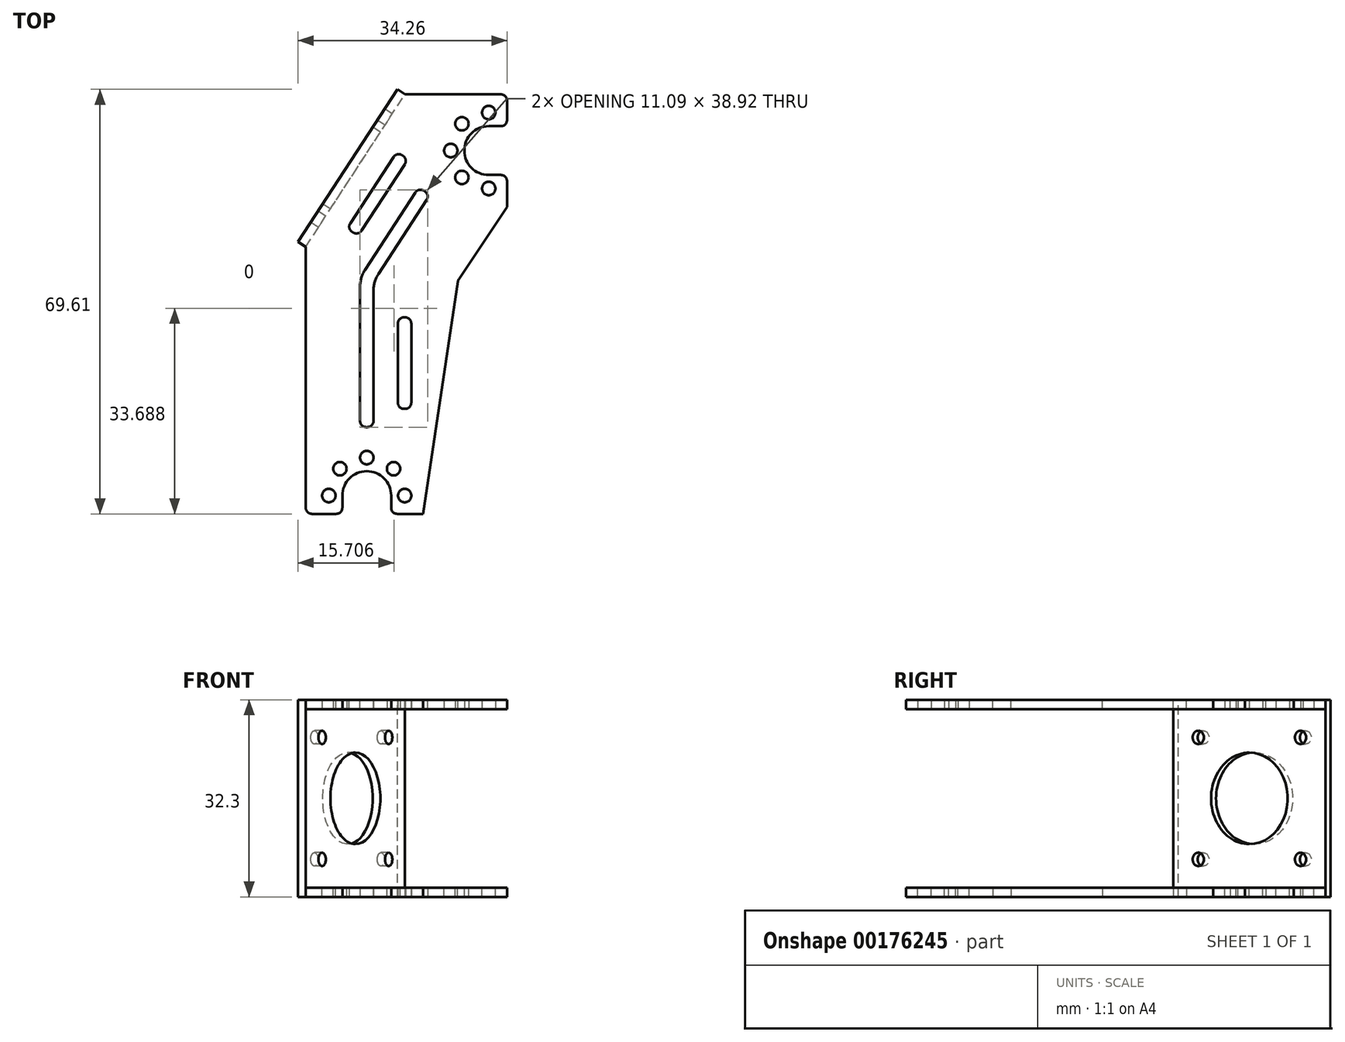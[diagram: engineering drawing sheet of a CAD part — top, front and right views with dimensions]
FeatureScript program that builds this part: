
annotation { "Feature Type Name" : "Feature", "Feature Type Description" : "" }
export const myFeature = defineFeature(function(context is Context, id is Id, definition is map)
    precondition{}
    {
        {
            var Q0;
            Q0=qCreatedBy(makeId("Top.planeOp"),FACE);
            var sketch = newSketch(context, id + "F0", { "sketchPlane" : qUnion([Q0])});
            skLineSegment(sketch, "E0.bottom", {"start": v(-16.5, 34.4) * mm, "end": v(16.5, 34.4) * mm});
            skLineSegment(sketch, "E0.top", {"start": v(-16.5, -34.4) * mm, "end": v(-10.5, -34.4) * mm});
            skLineSegment(sketch, "E0.left", {"start": v(-16.5, 34.4) * mm, "end": v(-16.5, -34.4) * mm});
            skLineSegment(sketch, "E0.right", {"start": v(16.5, 34.4) * mm, "end": v(16.5, 29.17) * mm});
            skPoint(sketch, "E0.middle", {"position": v(0, 0) * mm});
            skArc(sketch, "E1", {"start": v(13.5, 29.17) * mm, "mid": v(9.5, 25.17) * mm, "end": v(13.5, 21.17) * mm});
            skArc(sketch, "E2", {"start": v(-2.5, -31.4) * mm, "mid": v(-6.5, -27.4) * mm, "end": v(-10.5, -31.4) * mm});
            skLineSegment(sketch, "E3.bottom", {"start": v(9.1, 29.57) * mm, "end": v(17.9, 29.57) * mm, "construction": true});
            skLineSegment(sketch, "E3.top", {"start": v(9.1, 20.77) * mm, "end": v(17.9, 20.77) * mm, "construction": true});
            skLineSegment(sketch, "E3.left", {"start": v(9.1, 29.57) * mm, "end": v(9.1, 20.77) * mm, "construction": true});
            skLineSegment(sketch, "E3.right", {"start": v(17.9, 29.57) * mm, "end": v(17.9, 20.77) * mm, "construction": true});
            skCircle(sketch, "E4", {"center": v(9.1, 29.57) * mm, "radius": 1.1 * mm});
            skCircle(sketch, "E5.1.0", {"center": v(7.28, 25.17) * mm, "radius": 1.1 * mm});
            skCircle(sketch, "E5.2.0", {"center": v(9.1, 20.77) * mm, "radius": 1.1 * mm});
            skCircle(sketch, "E5.3.0", {"center": v(13.5, 18.95) * mm, "radius": 1.1 * mm});
            skCircle(sketch, "E5.7.0", {"center": v(13.5, 31.4) * mm, "radius": 1.1 * mm});
            skLineSegment(sketch, "E6.bottom", {"start": v(-10.9, -27) * mm, "end": v(-2.1, -27) * mm, "construction": true});
            skLineSegment(sketch, "E6.top", {"start": v(-10.9, -35.8) * mm, "end": v(-2.1, -35.8) * mm, "construction": true});
            skLineSegment(sketch, "E6.left", {"start": v(-10.9, -27) * mm, "end": v(-10.9, -35.8) * mm, "construction": true});
            skLineSegment(sketch, "E6.right", {"start": v(-2.1, -27) * mm, "end": v(-2.1, -35.8) * mm, "construction": true});
            skCircle(sketch, "E7", {"center": v(-2.1, -27) * mm, "radius": 1.1 * mm});
            skCircle(sketch, "E8.1.0", {"center": v(-6.5, -25.17) * mm, "radius": 1.1 * mm});
            skCircle(sketch, "E8.2.0", {"center": v(-10.9, -27) * mm, "radius": 1.1 * mm});
            skCircle(sketch, "E8.3.0", {"center": v(-12.72, -31.4) * mm, "radius": 1.1 * mm});
            skCircle(sketch, "E8.7.0", {"center": v(-0.28, -31.4) * mm, "radius": 1.1 * mm});
            skLineSegment(sketch, "E9", {"start": v(13.5, 29.17) * mm, "end": v(16.5, 29.17) * mm});
            skLineSegment(sketch, "E10", {"start": v(13.5, 21.17) * mm, "end": v(16.5, 21.17) * mm});
            skLineSegment(sketch, "E11.trimOffspring", {"start": v(16.5, 21.17) * mm, "end": v(16.5, -34.4) * mm});
            skLineSegment(sketch, "E12", {"start": v(-2.5, -31.4) * mm, "end": v(-2.5, -34.4) * mm});
            skLineSegment(sketch, "E13", {"start": v(-10.5, -31.4) * mm, "end": v(-10.5, -34.4) * mm});
            skLineSegment(sketch, "E14.trimOffspring", {"start": v(-2.5, -34.4) * mm, "end": v(16.5, -34.4) * mm});
            skSolve(sketch);
        }
        {
            var Q0;
            Q0=qSketchRegion(id+"F0",true);
            extrude(context, id + "F1", {"entities" : qUnion([Q0]), "depth" : 1.5 * mm});
        }
        {
            var Q0;
            Q0=makeQuery(id+"F1.opExtrude","CAP_FACE",FACE,{"disambiguationData":[OSD([sQuery(id+"F0.wireOp",EDGE,"E0.bottom"),sQuery(id+"F0.wireOp",EDGE,"E0.top"),sQuery(id+"F0.wireOp",EDGE,"E0.left"),sQuery(id+"F0.wireOp",EDGE,"E0.right"),sQuery(id+"F0.wireOp",EDGE,"E1"),sQuery(id+"F0.wireOp",EDGE,"E2"),sQuery(id+"F0.wireOp",EDGE,"E4"),sQuery(id+"F0.wireOp",EDGE,"E5.1.0"),sQuery(id+"F0.wireOp",EDGE,"E5.2.0"),sQuery(id+"F0.wireOp",EDGE,"E5.3.0"),sQuery(id+"F0.wireOp",EDGE,"E5.7.0"),sQuery(id+"F0.wireOp",EDGE,"E7"),sQuery(id+"F0.wireOp",EDGE,"E8.1.0"),sQuery(id+"F0.wireOp",EDGE,"E8.2.0"),sQuery(id+"F0.wireOp",EDGE,"E8.3.0"),sQuery(id+"F0.wireOp",EDGE,"E8.7.0"),sQuery(id+"F0.wireOp",EDGE,"E9"),sQuery(id+"F0.wireOp",EDGE,"E10"),sQuery(id+"F0.wireOp",EDGE,"E11.trimOffspring"),sQuery(id+"F0.wireOp",EDGE,"E12"),sQuery(id+"F0.wireOp",EDGE,"E13"),sQuery(id+"F0.wireOp",EDGE,"E14.trimOffspring")])],"isStart":false});
            var sketch = newSketch(context, id + "F2", { "sketchPlane" : qUnion([Q0])});
            skPoint(sketch, "E15", {"position": v(7.28, 25.17) * mm});
            skPoint(sketch, "E16", {"position": v(-0.28, -31.4) * mm});
            skLineSegment(sketch, "E17", {"start": v(-0.22, 34.4) * mm, "end": v(-16.5, 9.4) * mm});
            skPoint(sketch, "E18", {"position": v(13.5, 18.95) * mm});
            skLineSegment(sketch, "E19", {"start": v(16.5, 15.95) * mm, "end": v(8.5, 3.95) * mm});
            skLineSegment(sketch, "E20", {"start": v(8.5, 3.95) * mm, "end": v(2.72, -34.4) * mm});
            skPoint(sketch, "E21", {"position": v(13.5, 25.17) * mm});
            skPoint(sketch, "E22", {"position": v(-6.5, -31.4) * mm});
            skLineSegment(sketch, "E23", {"start": v(13.5, 25.17) * mm, "end": v(-6.5, -31.4) * mm, "construction": true});
            skLineSegment(sketch, "E24", {"start": v(0.31, -7.62) * mm, "end": v(-2.35, -15.17) * mm});
            skPoint(sketch, "E25", {"position": v(-1.02, -11.4) * mm});
            skLineSegment(sketch, "E26", {"start": v(1.59, -7.01) * mm, "end": v(2.06, -7.18) * mm});
            skLineSegment(sketch, "E27", {"start": v(-1.74, -16.44) * mm, "end": v(-1.27, -16.6) * mm});
            skLineSegment(sketch, "E28.MirrorCS", {"start": v(2.53, -7.35) * mm, "end": v(2.06, -7.18) * mm});
            skLineSegment(sketch, "E29.MirrorCS", {"start": v(3.14, -8.62) * mm, "end": v(0.48, -16.17) * mm});
            skLineSegment(sketch, "E30.MirrorCS", {"start": v(-0.8, -16.78) * mm, "end": v(-1.27, -16.6) * mm});
            skPoint(sketch, "E31.visualSharp", {"position": v(0.65, -6.68) * mm});
            skArc(sketch, "E31.filletArc", {"start": v(1.59, -7.01) * mm, "mid": v(0.83, -7.06) * mm, "end": v(0.31, -7.62) * mm});
            skPoint(sketch, "E32.visualSharp", {"position": v(-2.69, -16.1) * mm});
            skArc(sketch, "E32.filletArc", {"start": v(-2.35, -15.17) * mm, "mid": v(-2.31, -15.93) * mm, "end": v(-1.74, -16.44) * mm});
            skPoint(sketch, "E33.visualSharp", {"position": v(3.48, -7.68) * mm});
            skArc(sketch, "E33.filletArc", {"start": v(3.14, -8.62) * mm, "mid": v(3.1, -7.86) * mm, "end": v(2.53, -7.35) * mm});
            skPoint(sketch, "E34.visualSharp", {"position": v(0.14, -17.1) * mm});
            skArc(sketch, "E34.filletArc", {"start": v(-0.8, -16.78) * mm, "mid": v(-0.04, -16.74) * mm, "end": v(0.48, -16.17) * mm});
            skSolve(sketch);
        }
        {
            var Q0;
            {var subQ0=sQuery(id+"F2.wireOp",EDGE,"E19");Q0=makeQuery(id+"F2.imprint","IMPRINT",FACE,{"disambiguationData":[TD([[makeQuery(id+"F2.imprint","IMPRINT",EDGE,{"derivedFrom":subQ0}),1.0]])]});}
            var Q1;
            {var subQ0=sQuery(id+"F2.wireOp",EDGE,"E17");Q1=makeQuery(id+"F2.imprint","IMPRINT",FACE,{"disambiguationData":[TD([[makeQuery(id+"F2.imprint","IMPRINT",EDGE,{"derivedFrom":subQ0}),-1.0]])]});}
            extrude(context, id + "F3", {"entities" : qUnion([Q0, Q1]), "operationType" : NewBodyOperationType.REMOVE, "endBound" : BoundingType.UP_TO_NEXT, "oppositeDirection" : true, "depth" : 25 * mm});
        }
        {
            var Q0;
            Q0=makeQuery(id+"F1.opExtrude","CAP_FACE",FACE,{"disambiguationData":[OSD([sQuery(id+"F0.wireOp",EDGE,"E0.bottom"),sQuery(id+"F0.wireOp",EDGE,"E0.top"),sQuery(id+"F0.wireOp",EDGE,"E0.left"),sQuery(id+"F0.wireOp",EDGE,"E0.right"),sQuery(id+"F0.wireOp",EDGE,"E1"),sQuery(id+"F0.wireOp",EDGE,"E2"),sQuery(id+"F0.wireOp",EDGE,"E4"),sQuery(id+"F0.wireOp",EDGE,"E5.1.0"),sQuery(id+"F0.wireOp",EDGE,"E5.2.0"),sQuery(id+"F0.wireOp",EDGE,"E5.3.0"),sQuery(id+"F0.wireOp",EDGE,"E5.7.0"),sQuery(id+"F0.wireOp",EDGE,"E7"),sQuery(id+"F0.wireOp",EDGE,"E8.1.0"),sQuery(id+"F0.wireOp",EDGE,"E8.2.0"),sQuery(id+"F0.wireOp",EDGE,"E8.3.0"),sQuery(id+"F0.wireOp",EDGE,"E8.7.0"),sQuery(id+"F0.wireOp",EDGE,"E9"),sQuery(id+"F0.wireOp",EDGE,"E10"),sQuery(id+"F0.wireOp",EDGE,"E11.trimOffspring"),sQuery(id+"F0.wireOp",EDGE,"E12"),sQuery(id+"F0.wireOp",EDGE,"E13"),sQuery(id+"F0.wireOp",EDGE,"E14.trimOffspring")])],"isStart":false});
            var sketch = newSketch(context, id + "F4", { "sketchPlane" : qUnion([Q0])});
            skPoint(sketch, "E35", {"position": v(13.5, 25.17) * mm});
            skPoint(sketch, "E36", {"position": v(-6.5, -31.4) * mm});
            skPoint(sketch, "E37", {"position": v(7.28, 25.17) * mm});
            skPoint(sketch, "E38", {"position": v(-6.5, -25.17) * mm});
            skLineSegment(sketch, "E39", {"start": v(-6.5, -25.17) * mm, "end": v(-6.5, 4.01) * mm, "construction": true});
            skLineSegment(sketch, "E40", {"start": v(-6.5, 4.01) * mm, "end": v(7.28, 25.17) * mm, "construction": true});
            skLineSegment(sketch, "E41", {"start": v(1.49, 18.3) * mm, "end": v(-6.8, 5.58) * mm});
            skLineSegment(sketch, "E42", {"start": v(-7.6, 2.85) * mm, "end": v(-7.6, -19.17) * mm});
            skLineSegment(sketch, "E43", {"start": v(2.87, 18.59) * mm, "end": v(2.95, 18.53) * mm});
            skLineSegment(sketch, "E44", {"start": v(-6.6, -20.17) * mm, "end": v(-6.5, -20.17) * mm});
            skLineSegment(sketch, "E45.MirrorCS", {"start": v(-6.4, -20.17) * mm, "end": v(-6.5, -20.17) * mm});
            skLineSegment(sketch, "E46.MirrorCS", {"start": v(-5.4, 2.2) * mm, "end": v(-5.4, -19.17) * mm});
            skLineSegment(sketch, "E47.MirrorCS", {"start": v(3.33, 17.1) * mm, "end": v(-4.6, 4.93) * mm});
            skLineSegment(sketch, "E48.MirrorCS", {"start": v(3.04, 18.48) * mm, "end": v(2.95, 18.53) * mm});
            skPoint(sketch, "E49.orphan", {"position": v(-5.4, 4.34) * mm});
            skPoint(sketch, "E50.orphan", {"position": v(-5.76, 3.14) * mm});
            skPoint(sketch, "E51.visualSharp", {"position": v(2.03, 19.13) * mm});
            skArc(sketch, "E51.filletArc", {"start": v(2.87, 18.59) * mm, "mid": v(2.12, 18.73) * mm, "end": v(1.49, 18.3) * mm});
            skPoint(sketch, "E52.visualSharp", {"position": v(3.88, 17.93) * mm});
            skArc(sketch, "E52.filletArc", {"start": v(3.33, 17.1) * mm, "mid": v(3.47, 17.85) * mm, "end": v(3.04, 18.48) * mm});
            skPoint(sketch, "E53.visualSharp", {"position": v(-7.6, -20.17) * mm});
            skArc(sketch, "E53.filletArc", {"start": v(-7.6, -19.17) * mm, "mid": v(-7.3, -19.88) * mm, "end": v(-6.6, -20.17) * mm});
            skPoint(sketch, "E54.visualSharp", {"position": v(-5.4, -20.17) * mm});
            skArc(sketch, "E54.filletArc", {"start": v(-6.4, -20.17) * mm, "mid": v(-5.7, -19.88) * mm, "end": v(-5.4, -19.17) * mm});
            skPoint(sketch, "E55.visualSharp", {"position": v(-7.6, 4.34) * mm});
            skArc(sketch, "E55.filletArc", {"start": v(-6.8, 5.58) * mm, "mid": v(-7.4, 4.28) * mm, "end": v(-7.6, 2.85) * mm});
            skPoint(sketch, "E56.visualSharp", {"position": v(-5.4, 3.69) * mm});
            skArc(sketch, "E56.filletArc", {"start": v(-4.6, 4.93) * mm, "mid": v(-5.2, 3.62) * mm, "end": v(-5.4, 2.2) * mm});
            skLineSegment(sketch, "E57", {"start": v(-0.27, 22.93) * mm, "end": v(-7.36, 12.03) * mm});
            skLineSegment(sketch, "E58", {"start": v(-8.75, 11.74) * mm, "end": v(-8.91, 11.85) * mm});
            skLineSegment(sketch, "E59", {"start": v(-0.56, 24.31) * mm, "end": v(-0.73, 24.42) * mm});
            skLineSegment(sketch, "E60", {"start": v(-2.11, 24.13) * mm, "end": v(-9.2, 13.23) * mm});
            skPoint(sketch, "E61.visualSharp", {"position": v(-1.57, 24.97) * mm});
            skArc(sketch, "E61.filletArc", {"start": v(-0.73, 24.42) * mm, "mid": v(-1.48, 24.56) * mm, "end": v(-2.11, 24.13) * mm});
            skPoint(sketch, "E62.visualSharp", {"position": v(-9.75, 12.4) * mm});
            skArc(sketch, "E62.filletArc", {"start": v(-9.2, 13.23) * mm, "mid": v(-9.35, 12.48) * mm, "end": v(-8.91, 11.85) * mm});
            skPoint(sketch, "E63.visualSharp", {"position": v(0.28, 23.77) * mm});
            skArc(sketch, "E63.filletArc", {"start": v(-0.27, 22.93) * mm, "mid": v(-0.13, 23.68) * mm, "end": v(-0.56, 24.31) * mm});
            skPoint(sketch, "E64.visualSharp", {"position": v(-7.9, 11.2) * mm});
            skArc(sketch, "E64.filletArc", {"start": v(-8.75, 11.74) * mm, "mid": v(-8, 11.6) * mm, "end": v(-7.36, 12.03) * mm});
            skLineSegment(sketch, "E65.bottom", {"start": v(-0.4, -2.17) * mm, "end": v(-0.2, -2.17) * mm});
            skLineSegment(sketch, "E65.top", {"start": v(-0.4, -17.17) * mm, "end": v(-0.2, -17.17) * mm});
            skLineSegment(sketch, "E65.left", {"start": v(-1.4, -3.17) * mm, "end": v(-1.4, -16.17) * mm});
            skLineSegment(sketch, "E65.right", {"start": v(0.8, -3.17) * mm, "end": v(0.8, -16.17) * mm});
            skPoint(sketch, "E65.middle", {"position": v(-0.3, -9.67) * mm});
            skPoint(sketch, "E66.visualSharp", {"position": v(-1.4, -2.17) * mm});
            skArc(sketch, "E66.filletArc", {"start": v(-0.4, -2.17) * mm, "mid": v(-1.1, -2.47) * mm, "end": v(-1.4, -3.17) * mm});
            skPoint(sketch, "E67.visualSharp", {"position": v(-1.4, -17.17) * mm});
            skArc(sketch, "E67.filletArc", {"start": v(-1.4, -16.17) * mm, "mid": v(-1.1, -16.88) * mm, "end": v(-0.4, -17.17) * mm});
            skPoint(sketch, "E68.visualSharp", {"position": v(0.8, -17.17) * mm});
            skArc(sketch, "E68.filletArc", {"start": v(-0.2, -17.17) * mm, "mid": v(0.5, -16.88) * mm, "end": v(0.8, -16.17) * mm});
            skPoint(sketch, "E69.visualSharp", {"position": v(0.8, -2.17) * mm});
            skArc(sketch, "E69.filletArc", {"start": v(0.8, -3.17) * mm, "mid": v(0.5, -2.47) * mm, "end": v(-0.2, -2.17) * mm});
            skLineSegment(sketch, "E70.MirrorCS", {"start": v(1.48, 5.08) * mm, "end": v(1.64, 4.98) * mm, "construction": true});
            skLineSegment(sketch, "E71.MirrorCS", {"start": v(9.66, 17.65) * mm, "end": v(9.83, 17.55) * mm, "construction": true});
            skArc(sketch, "E72.MirrorCS", {"start": v(3.03, 5.27) * mm, "mid": v(2.4, 4.83) * mm, "end": v(1.64, 4.98) * mm, "construction": true});
            skArc(sketch, "E73.MirrorCS", {"start": v(8.28, 17.36) * mm, "mid": v(8.9, 17.8) * mm, "end": v(9.66, 17.65) * mm, "construction": true});
            skArc(sketch, "E74.MirrorCS", {"start": v(9.83, 17.55) * mm, "mid": v(10.26, 16.91) * mm, "end": v(10.12, 16.16) * mm, "construction": true});
            skArc(sketch, "E75.MirrorCS", {"start": v(1.48, 5.08) * mm, "mid": v(1.04, 5.72) * mm, "end": v(1.18, 6.47) * mm, "construction": true});
            skLineSegment(sketch, "E76.MirrorCS", {"start": v(10.12, 16.16) * mm, "end": v(3.03, 5.27) * mm, "construction": true});
            skPoint(sketch, "E77.MirrorP", {"position": v(10.67, 17) * mm});
            skPoint(sketch, "E78.MirrorP", {"position": v(8.82, 18.2) * mm});
            skLineSegment(sketch, "E79.MirrorCS", {"start": v(8.28, 17.36) * mm, "end": v(1.18, 6.47) * mm, "construction": true});
            skPoint(sketch, "E80.MirrorP", {"position": v(2.48, 4.43) * mm});
            skPoint(sketch, "E81.MirrorP", {"position": v(0.64, 5.63) * mm});
            skLineSegment(sketch, "E82.MirrorCS", {"start": v(-12.6, -17.17) * mm, "end": v(-12.8, -17.17) * mm, "construction": true});
            skLineSegment(sketch, "E83.MirrorCS", {"start": v(-12.6, -2.17) * mm, "end": v(-12.8, -2.17) * mm, "construction": true});
            skArc(sketch, "E84.MirrorCS", {"start": v(-12.8, -17.17) * mm, "mid": v(-13.5, -16.88) * mm, "end": v(-13.8, -16.17) * mm, "construction": true});
            skArc(sketch, "E85.MirrorCS", {"start": v(-13.8, -3.17) * mm, "mid": v(-13.5, -2.47) * mm, "end": v(-12.8, -2.17) * mm, "construction": true});
            skArc(sketch, "E86.MirrorCS", {"start": v(-12.6, -2.17) * mm, "mid": v(-11.9, -2.47) * mm, "end": v(-11.6, -3.17) * mm, "construction": true});
            skArc(sketch, "E87.MirrorCS", {"start": v(-11.6, -16.17) * mm, "mid": v(-11.9, -16.88) * mm, "end": v(-12.6, -17.17) * mm, "construction": true});
            skPoint(sketch, "E88.MirrorP", {"position": v(-13.8, -17.17) * mm});
            skPoint(sketch, "E89.MirrorP", {"position": v(-13.8, -2.17) * mm});
            skLineSegment(sketch, "E90.MirrorCS", {"start": v(-11.6, -3.17) * mm, "end": v(-11.6, -16.17) * mm, "construction": true});
            skPoint(sketch, "E91.MirrorP", {"position": v(-12.7, -9.67) * mm});
            skPoint(sketch, "E92.MirrorP", {"position": v(-11.6, -2.17) * mm});
            skPoint(sketch, "E93.MirrorP", {"position": v(-11.6, -17.17) * mm});
            skLineSegment(sketch, "E94.MirrorCS", {"start": v(-13.8, -3.17) * mm, "end": v(-13.8, -16.17) * mm, "construction": true});
            skPoint(sketch, "E95.0.1.0", {"position": v(-11.6, -7.17) * mm});
            skPoint(sketch, "E95.0.1.1", {"position": v(-11.6, 7.83) * mm});
            skPoint(sketch, "E95.0.1.2", {"position": v(-12.7, 0.33) * mm});
            skLineSegment(sketch, "E95.0.1.3", {"start": v(-13.8, 6.83) * mm, "end": v(-13.8, -6.17) * mm});
            skPoint(sketch, "E95.0.1.4", {"position": v(-13.8, -7.17) * mm});
            skLineSegment(sketch, "E95.0.1.5", {"start": v(-11.6, 6.83) * mm, "end": v(-11.6, -6.17) * mm});
            skPoint(sketch, "E95.0.1.6", {"position": v(-13.8, 7.83) * mm});
            skArc(sketch, "E95.0.1.7", {"start": v(-12.8, -7.17) * mm, "mid": v(-13.5, -6.88) * mm, "end": v(-13.8, -6.17) * mm});
            skArc(sketch, "E95.0.1.8", {"start": v(-13.8, 6.83) * mm, "mid": v(-13.5, 7.53) * mm, "end": v(-12.8, 7.83) * mm});
            skArc(sketch, "E95.0.1.9", {"start": v(-12.6, 7.83) * mm, "mid": v(-11.9, 7.53) * mm, "end": v(-11.6, 6.83) * mm});
            skArc(sketch, "E95.0.1.10", {"start": v(-11.6, -6.17) * mm, "mid": v(-11.9, -6.88) * mm, "end": v(-12.6, -7.17) * mm});
            skLineSegment(sketch, "E95.0.1.11", {"start": v(-12.6, 7.83) * mm, "end": v(-12.8, 7.83) * mm});
            skLineSegment(sketch, "E95.0.1.12", {"start": v(-12.6, -7.17) * mm, "end": v(-12.8, -7.17) * mm});
            skLineSegment(sketch, "E95.direction1", {"start": v(-13.8, -17.17) * mm, "end": v(11.2, -17.17) * mm, "construction": true});
            skLineSegment(sketch, "E95.direction2", {"start": v(-13.8, -17.17) * mm, "end": v(-13.8, -7.17) * mm, "construction": true});
            skLineSegment(sketch, "E96.1.0.0", {"start": v(2.82, 8.98) * mm, "end": v(-4.27, -1.91) * mm});
            skArc(sketch, "E96.1.0.1", {"start": v(2.82, 8.98) * mm, "mid": v(3.45, 9.41) * mm, "end": v(4.2, 9.27) * mm});
            skArc(sketch, "E96.1.0.2", {"start": v(4.37, 9.17) * mm, "mid": v(4.8, 8.53) * mm, "end": v(4.66, 7.78) * mm});
            skLineSegment(sketch, "E96.1.0.3", {"start": v(4.2, 9.27) * mm, "end": v(4.37, 9.17) * mm});
            skLineSegment(sketch, "E96.1.0.4", {"start": v(4.66, 7.78) * mm, "end": v(-2.43, -3.11) * mm});
            skArc(sketch, "E96.1.0.5", {"start": v(-3.98, -3.3) * mm, "mid": v(-4.41, -2.66) * mm, "end": v(-4.27, -1.91) * mm});
            skLineSegment(sketch, "E96.1.0.6", {"start": v(-3.98, -3.3) * mm, "end": v(-3.81, -3.4) * mm});
            skArc(sketch, "E96.1.0.7", {"start": v(-2.43, -3.11) * mm, "mid": v(-3.06, -3.55) * mm, "end": v(-3.81, -3.4) * mm});
            skLineSegment(sketch, "E96.direction1", {"start": v(-3.98, -3.3) * mm, "end": v(1.48, 5.08) * mm, "construction": true});
            skSolve(sketch);
        }
        {
            var Q0;
            Q0=makeQuery(id+"F4.imprint","IMPRINT",FACE,{"disambiguationData":[TD([[makeQuery(id+"F4.imprint","IMPRINT",EDGE,{"derivedFrom":sQuery(id+"F4.wireOp",EDGE,"E57")}),-1.0]])]});
            var Q1;
            Q1=makeQuery(id+"F4.imprint","IMPRINT",FACE,{"disambiguationData":[TD([[makeQuery(id+"F4.imprint","IMPRINT",EDGE,{"derivedFrom":sQuery(id+"F4.wireOp",EDGE,"E41")}),1.0]])]});
            var Q2;
            Q2=makeQuery(id+"F4.imprint","IMPRINT",FACE,{"disambiguationData":[TD([[makeQuery(id+"F4.imprint","IMPRINT",EDGE,{"derivedFrom":sQuery(id+"F4.wireOp",EDGE,"E65.bottom")}),-1.0]])]});
            extrude(context, id + "F5", {"entities" : qUnion([Q0, Q1, Q2]), "operationType" : NewBodyOperationType.REMOVE, "endBound" : BoundingType.UP_TO_NEXT, "oppositeDirection" : true, "depth" : 25 * mm});
        }
        {
            var Q0;
            Q0=makeQuery(id+"F1.opExtrude","SWEPT_EDGE",EDGE,{"disambiguationData":[OSD([sQuery(id+"F0.wireOp",EDGE,"E0.top"),sQuery(id+"F0.wireOp",EDGE,"E0.left")])]});
            var Q1;
            Q1=makeQuery(id+"F1.opExtrude","SWEPT_EDGE",EDGE,{"disambiguationData":[OSD([sQuery(id+"F0.wireOp",EDGE,"E0.top"),sQuery(id+"F0.wireOp",EDGE,"E13")])]});
            var Q2;
            Q2=makeQuery(id+"F1.opExtrude","SWEPT_EDGE",EDGE,{"disambiguationData":[OSD([sQuery(id+"F0.wireOp",EDGE,"E12"),sQuery(id+"F0.wireOp",EDGE,"E14.trimOffspring")])]});
            var Q3;
            Q3=makeQuery(id+"F3.boolean.opBoolean","COPY",EDGE,{"derivedFrom":makeQuery(id+"F3.opExtrude","SWEPT_EDGE",EDGE,{"disambiguationData":[OSD([sQuery(id+"F0.wireOp",EDGE,"E14.trimOffspring"),sQuery(id+"F2.wireOp",EDGE,"E20")])]})});
            var Q4;
            Q4=makeQuery(id+"F3.boolean.opBoolean","COPY",EDGE,{"derivedFrom":makeQuery(id+"F3.opExtrude","SWEPT_EDGE",EDGE,{"disambiguationData":[OSD([sQuery(id+"F2.wireOp",EDGE,"E19"),sQuery(id+"F2.wireOp",EDGE,"E20")])]})});
            var Q5;
            Q5=makeQuery(id+"F3.boolean.opBoolean","COPY",EDGE,{"derivedFrom":makeQuery(id+"F3.opExtrude","SWEPT_EDGE",EDGE,{"disambiguationData":[OSD([sQuery(id+"F0.wireOp",EDGE,"E11.trimOffspring"),sQuery(id+"F2.wireOp",EDGE,"E19")])]})});
            var Q6;
            Q6=makeQuery(id+"F1.opExtrude","SWEPT_EDGE",EDGE,{"disambiguationData":[OSD([sQuery(id+"F0.wireOp",EDGE,"E0.bottom"),sQuery(id+"F0.wireOp",EDGE,"E0.right")])]});
            var Q7;
            Q7=makeQuery(id+"F1.opExtrude","SWEPT_EDGE",EDGE,{"disambiguationData":[OSD([sQuery(id+"F0.wireOp",EDGE,"E10"),sQuery(id+"F0.wireOp",EDGE,"E11.trimOffspring")])]});
            var Q8;
            Q8=makeQuery(id+"F1.opExtrude","SWEPT_EDGE",EDGE,{"disambiguationData":[OSD([sQuery(id+"F0.wireOp",EDGE,"E0.right"),sQuery(id+"F0.wireOp",EDGE,"E9")])]});
            fillet(context, id + "F6", {"entities" : qUnion([Q0, Q1, Q2, Q3, Q4, Q5, Q6, Q7, Q8]), "radius" : 1 * mm, "tangentPropagation" : true, "allowEdgeOverflow" : false});
        }
        {
            var Q0;
            Q0=makeQuery(id+"F1.opExtrude","CAP_FACE",FACE,{"disambiguationData":[OSD([sQuery(id+"F0.wireOp",EDGE,"E0.bottom"),sQuery(id+"F0.wireOp",EDGE,"E0.top"),sQuery(id+"F0.wireOp",EDGE,"E0.left"),sQuery(id+"F0.wireOp",EDGE,"E0.right"),sQuery(id+"F0.wireOp",EDGE,"E1"),sQuery(id+"F0.wireOp",EDGE,"E2"),sQuery(id+"F0.wireOp",EDGE,"E4"),sQuery(id+"F0.wireOp",EDGE,"E5.1.0"),sQuery(id+"F0.wireOp",EDGE,"E5.2.0"),sQuery(id+"F0.wireOp",EDGE,"E5.3.0"),sQuery(id+"F0.wireOp",EDGE,"E5.7.0"),sQuery(id+"F0.wireOp",EDGE,"E7"),sQuery(id+"F0.wireOp",EDGE,"E8.1.0"),sQuery(id+"F0.wireOp",EDGE,"E8.2.0"),sQuery(id+"F0.wireOp",EDGE,"E8.3.0"),sQuery(id+"F0.wireOp",EDGE,"E8.7.0"),sQuery(id+"F0.wireOp",EDGE,"E9"),sQuery(id+"F0.wireOp",EDGE,"E10"),sQuery(id+"F0.wireOp",EDGE,"E11.trimOffspring"),sQuery(id+"F0.wireOp",EDGE,"E12"),sQuery(id+"F0.wireOp",EDGE,"E13"),sQuery(id+"F0.wireOp",EDGE,"E14.trimOffspring")])],"isStart":false});
            var sketch = newSketch(context, id + "F7", { "sketchPlane" : qUnion([Q0])});
            skLineSegment(sketch, "E97", {"start": v(-16.5, 9.4) * mm, "end": v(-0.22, 34.4) * mm});
            skLineSegment(sketch, "E98", {"start": v(-0.22, 34.4) * mm, "end": v(-1.48, 35.21) * mm});
            skLineSegment(sketch, "E99", {"start": v(-1.48, 35.21) * mm, "end": v(-17.76, 10.21) * mm});
            skLineSegment(sketch, "E100", {"start": v(-17.76, 10.21) * mm, "end": v(-16.5, 9.4) * mm});
            skSolve(sketch);
        }
        {
            var Q0;
            Q0=qSketchRegion(id+"F7",true);
            extrude(context, id + "F8", {"entities" : qUnion([Q0]), "operationType" : NewBodyOperationType.ADD, "oppositeDirection" : true, "depth" : (1.5 + 29.3 / 2) * mm});
        }
        {
            var Q0;
            Q0=qCreatedBy(makeId("Top.planeOp"),FACE);
            cPlane(context, id + "F9", {"entities" : qUnion([Q0]), "cplaneType" : CPlaneType.OFFSET, "offset" : (29.3 / 2) * mm, "oppositeDirection" : true, "width" : 150 * mm, "height" : 150 * mm});
        }
        {
            var Q0;
            Q0=makeQuery(id+"F1.opExtrude","SWEPT_BODY",BODY,{"disambiguationData":[OSD([sQuery(id+"F0.wireOp",EDGE,"E0.bottom"),sQuery(id+"F0.wireOp",EDGE,"E0.top"),sQuery(id+"F0.wireOp",EDGE,"E0.left"),sQuery(id+"F0.wireOp",EDGE,"E0.right"),sQuery(id+"F0.wireOp",EDGE,"E1"),sQuery(id+"F0.wireOp",EDGE,"E2"),sQuery(id+"F0.wireOp",EDGE,"E4"),sQuery(id+"F0.wireOp",EDGE,"E5.1.0"),sQuery(id+"F0.wireOp",EDGE,"E5.2.0"),sQuery(id+"F0.wireOp",EDGE,"E5.3.0"),sQuery(id+"F0.wireOp",EDGE,"E5.7.0"),sQuery(id+"F0.wireOp",EDGE,"E7"),sQuery(id+"F0.wireOp",EDGE,"E8.1.0"),sQuery(id+"F0.wireOp",EDGE,"E8.2.0"),sQuery(id+"F0.wireOp",EDGE,"E8.3.0"),sQuery(id+"F0.wireOp",EDGE,"E8.7.0"),sQuery(id+"F0.wireOp",EDGE,"E9"),sQuery(id+"F0.wireOp",EDGE,"E10"),sQuery(id+"F0.wireOp",EDGE,"E11.trimOffspring"),sQuery(id+"F0.wireOp",EDGE,"E12"),sQuery(id+"F0.wireOp",EDGE,"E13"),sQuery(id+"F0.wireOp",EDGE,"E14.trimOffspring")])]});
            var Q1;
            Q1=qCreatedBy(id+"F9.planeOp",FACE);
            mirror(context, id + "F10", {"operationType" : NewBodyOperationType.ADD, "entities" : qUnion([Q0]), "mirrorPlane" : qUnion([Q1])});
        }
        {
            var Q0;
            {var subQ0=makeQuery(id+"F8.opExtrude","SWEPT_FACE",FACE,{"disambiguationData":[OSD([sQuery(id+"F7.wireOp",EDGE,"E99")])]});Q0=makeQuery(id+"F10.boolean.opBoolean","MERGE",FACE,{"derivedFrom":[subQ0,makeQuery(id+"F10.opPattern","COPY",FACE,{"derivedFrom":subQ0,"instanceName":"1"})]});}
            var sketch = newSketch(context, id + "F11", { "sketchPlane" : qUnion([Q0])});
            skLineSegment(sketch, "E101", {"start": v(-13.79, -30.8) * mm, "end": v(-13.79, 1.5) * mm, "construction": true});
            skLineSegment(sketch, "E102.bottom", {"start": v(-23.79, -24.65) * mm, "end": v(-3.79, -24.65) * mm, "construction": true});
            skLineSegment(sketch, "E102.top", {"start": v(-23.79, -4.65) * mm, "end": v(-3.79, -4.65) * mm, "construction": true});
            skLineSegment(sketch, "E102.left", {"start": v(-23.79, -24.65) * mm, "end": v(-23.79, -4.65) * mm, "construction": true});
            skLineSegment(sketch, "E102.right", {"start": v(-3.79, -24.65) * mm, "end": v(-3.79, -4.65) * mm, "construction": true});
            skPoint(sketch, "E102.middle", {"position": v(-13.79, -14.65) * mm});
            skCircle(sketch, "E103", {"center": v(-23.79, -24.65) * mm, "radius": 1.1 * mm});
            skCircle(sketch, "E104.MirrorC", {"center": v(-23.79, -4.65) * mm, "radius": 1.1 * mm});
            skCircle(sketch, "E105.MirrorC", {"center": v(-3.79, -24.65) * mm, "radius": 1.1 * mm});
            skCircle(sketch, "E106.MirrorC", {"center": v(-3.79, -4.65) * mm, "radius": 1.1 * mm});
            skCircle(sketch, "E107", {"center": v(-13.79, -14.65) * mm, "radius": 7.5 * mm});
            skSolve(sketch);
        }
        {
            var Q0;
            Q0=qSketchRegion(id+"F11",true);
            extrude(context, id + "F12", {"entities" : qUnion([Q0]), "operationType" : NewBodyOperationType.REMOVE, "endBound" : BoundingType.UP_TO_NEXT, "oppositeDirection" : true, "depth" : 25 * mm});
        }
    });
